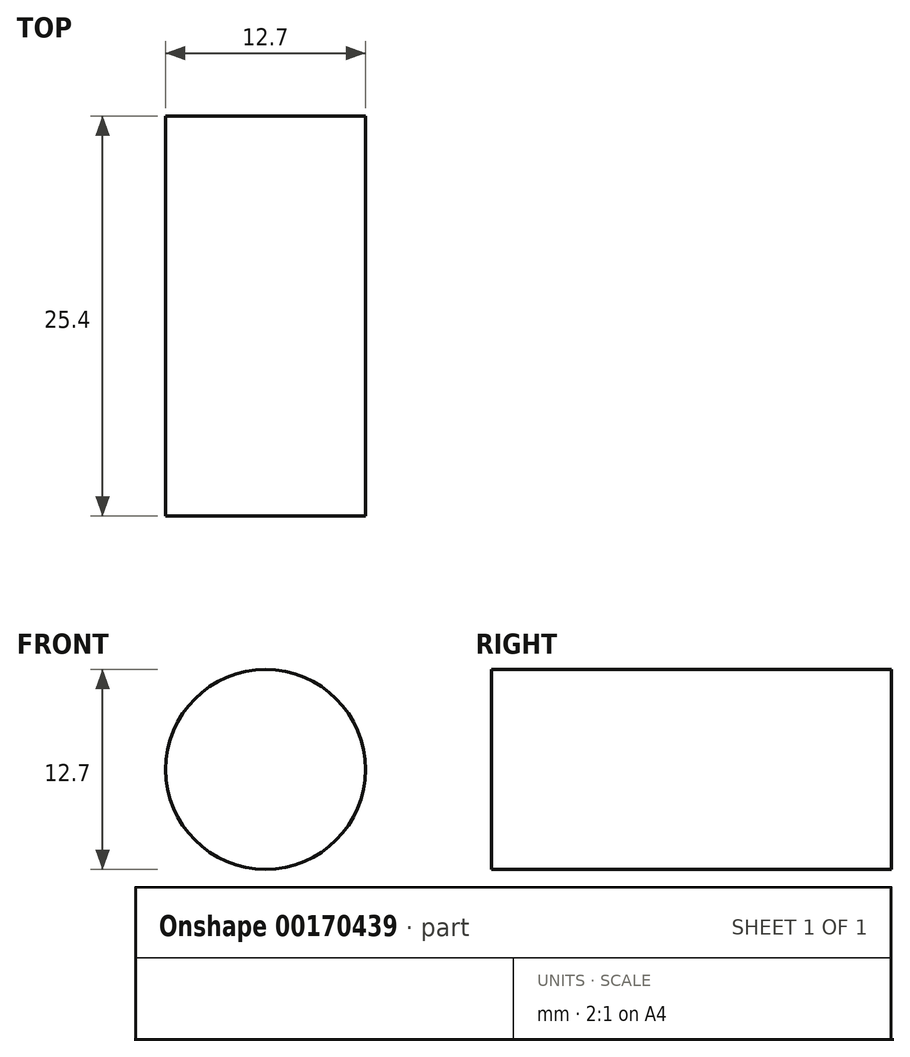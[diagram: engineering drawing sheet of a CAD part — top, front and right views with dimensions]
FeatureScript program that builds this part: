
annotation { "Feature Type Name" : "Feature", "Feature Type Description" : "" }
export const myFeature = defineFeature(function(context is Context, id is Id, definition is map)
    precondition{}
    {
        {
            var Q0;
            Q0=qCreatedBy(makeId("Front.planeOp"),FACE);
            var sketch = newSketch(context, id + "F0", { "sketchPlane" : qUnion([Q0])});
            skCircle(sketch, "E0", {"center": v(0, 0) * mm, "radius": 6.35 * mm});
            skSolve(sketch);
        }
        {
            var Q0;
            Q0 = qSketchRegion(id + "F0", true);
            extrude(context, id + "F1", {"entities" : qUnion([Q0]), "depth" : 25.4 * mm});
        }
    });
